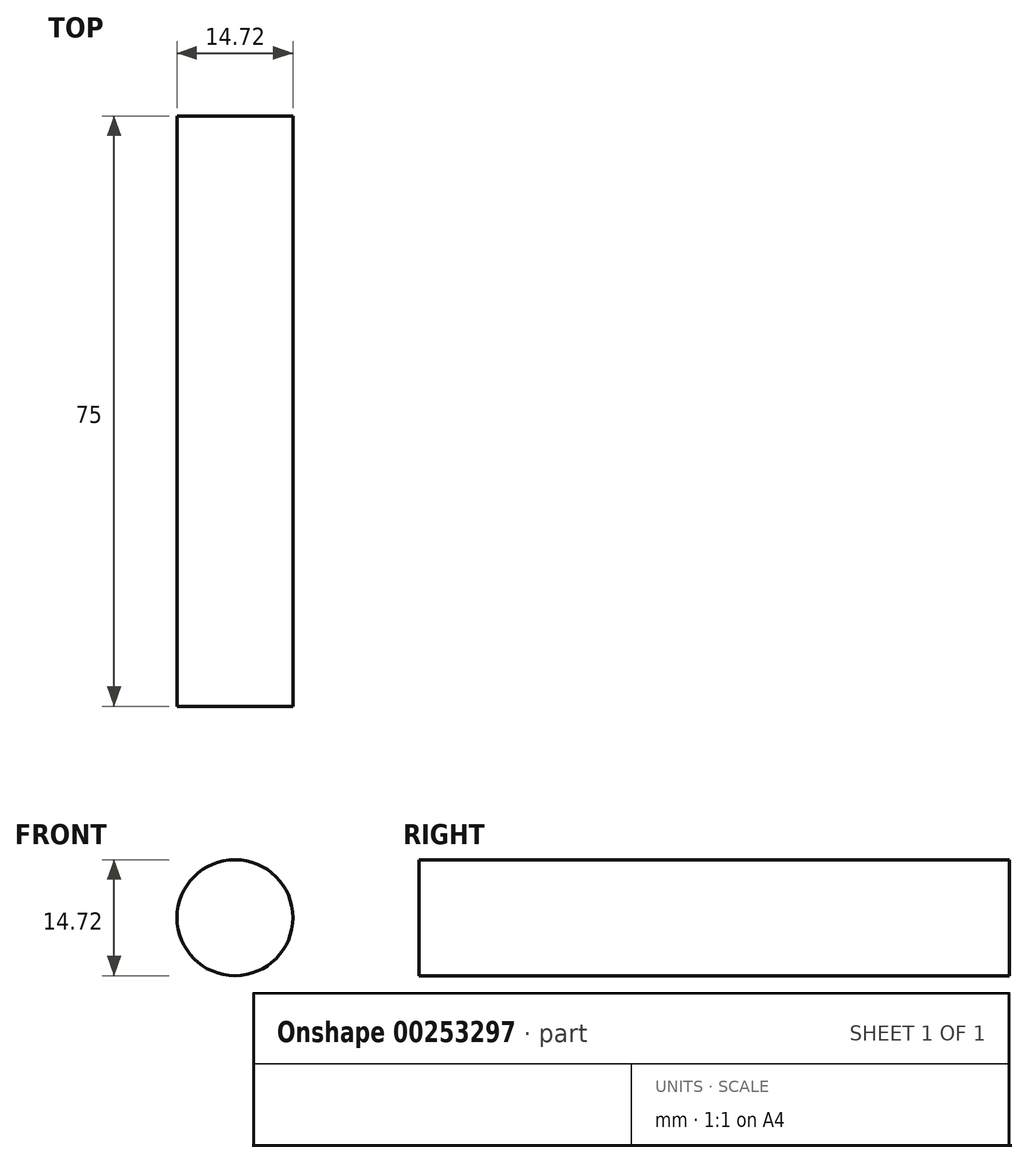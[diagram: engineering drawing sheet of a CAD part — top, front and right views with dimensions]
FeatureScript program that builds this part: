
annotation { "Feature Type Name" : "Feature", "Feature Type Description" : "" }
export const myFeature = defineFeature(function(context is Context, id is Id, definition is map)
    precondition{}
    {
        {
            var Q0;
            Q0=qCreatedBy(makeId("Front.planeOp"),FACE);
            var sketch = newSketch(context, id + "F0", { "sketchPlane" : qUnion([Q0])});
            skCircle(sketch, "E0", {"center": v(0, 0) * mm, "radius": 7.36 * mm});
            skSolve(sketch);
        }
        {
            var Q0;
            Q0=makeQuery(id+"F0.imprint","IMPRINT",FACE,{"disambiguationData":[TD([[makeQuery(id+"F0.imprint","IMPRINT",EDGE,{"derivedFrom":sQuery(id+"F0.wireOp",EDGE,"E0")}),1.0]])]});
            extrude(context, id + "F1", {"entities" : qUnion([Q0]), "depth" : 75 * mm});
        }
    });
